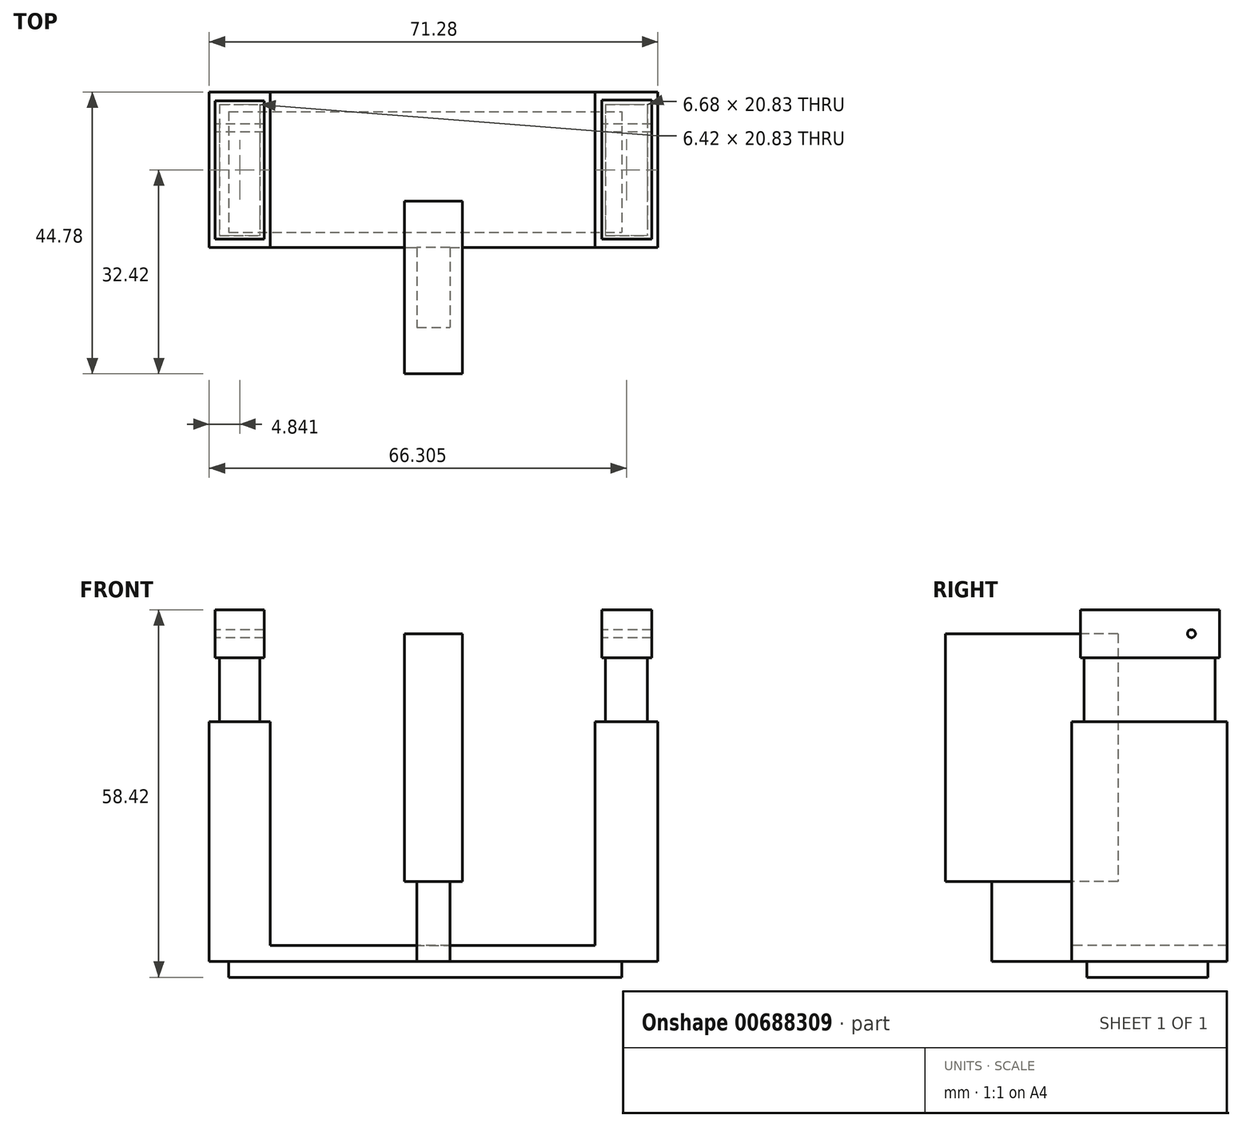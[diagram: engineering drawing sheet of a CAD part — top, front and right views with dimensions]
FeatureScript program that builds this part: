
annotation { "Feature Type Name" : "Feature", "Feature Type Description" : "" }
export const myFeature = defineFeature(function(context is Context, id is Id, definition is map)
    precondition{}
    {
        {
            var Q0;
            Q0=qCreatedBy(makeId("Top.planeOp"),FACE);
            var sketch = newSketch(context, id + "F0", { "sketchPlane" : qUnion([Q0])});
            skLineSegment(sketch, "E0.bottom", {"start": v(0, 0) * mm, "end": v(71.28, 0) * mm});
            skLineSegment(sketch, "E0.top", {"start": v(0, -24.72) * mm, "end": v(33.02, -24.72) * mm});
            skLineSegment(sketch, "E0.left", {"start": v(0, 0) * mm, "end": v(0, -24.72) * mm});
            skLineSegment(sketch, "E0.right", {"start": v(71.28, 0) * mm, "end": v(71.28, -24.72) * mm});
            skLineSegment(sketch, "E1.bottom", {"start": v(3.1, -3.1) * mm, "end": v(65.55, -3.1) * mm});
            skLineSegment(sketch, "E1.top", {"start": v(3.1, -22.32) * mm, "end": v(65.55, -22.32) * mm});
            skLineSegment(sketch, "E1.left", {"start": v(3.1, -3.1) * mm, "end": v(3.1, -22.32) * mm});
            skLineSegment(sketch, "E1.right", {"start": v(65.55, -3.1) * mm, "end": v(65.55, -22.32) * mm});
            skLineSegment(sketch, "E2.bottom", {"start": v(33.02, -24.72) * mm, "end": v(33.02, -24.72) * mm});
            skLineSegment(sketch, "E2.top", {"start": v(33.02, -37.42) * mm, "end": v(38.26, -37.42) * mm});
            skLineSegment(sketch, "E2.left", {"start": v(33.02, -24.72) * mm, "end": v(33.02, -37.42) * mm});
            skLineSegment(sketch, "E2.right", {"start": v(38.26, -24.72) * mm, "end": v(38.26, -37.42) * mm});
            skLineSegment(sketch, "E3", {"start": v(38.26, -24.72) * mm, "end": v(71.28, -24.72) * mm});
            skLineSegment(sketch, "E4", {"start": v(33.02, -24.72) * mm, "end": v(38.26, -24.72) * mm});
            skSolve(sketch);
        }
        {
            var Q0;
            Q0=makeQuery(id+"F0.imprint","IMPRINT",FACE,{"disambiguationData":[TD([[makeQuery(id+"F0.imprint","IMPRINT",EDGE,{"derivedFrom":sQuery(id+"F0.wireOp",EDGE,"E1.bottom")}),-1.0]])]});
            extrude(context, id + "F1", {"entities" : qUnion([Q0]), "depth" : 2.54 * mm, "offsetDistance" : 25.4 * mm});
        }
        {
            var Q0;
            Q0 = qSketchRegion(id + "F0", true);
            var Q1;
            Q1=makeQuery(id+"F1.opExtrude","CAP_FACE",FACE,{"disambiguationData":[OSD([sQuery(id+"F0.wireOp",EDGE,"E1.bottom"),sQuery(id+"F0.wireOp",EDGE,"E1.top"),sQuery(id+"F0.wireOp",EDGE,"E1.left"),sQuery(id+"F0.wireOp",EDGE,"E1.right")])],"isStart":true});
            extrude(context, id + "F2", {"entities" : qUnion([Q0, Q1]), "operationType" : NewBodyOperationType.ADD, "depth" : 2.54 * mm, "offsetDistance" : 25.4 * mm});
        }
        {
            var Q0;
            Q0=makeQuery(id+"F0.imprint","IMPRINT",FACE,{"disambiguationData":[TD([[makeQuery(id+"F0.imprint","IMPRINT",EDGE,{"derivedFrom":sQuery(id+"F0.wireOp",EDGE,"E1.bottom")}),-1.0]])]});
            extrude(context, id + "F3", {"entities" : qUnion([Q0]), "operationType" : NewBodyOperationType.ADD, "oppositeDirection" : true, "depth" : 2.54 * mm, "offsetDistance" : 25.4 * mm});
        }
        {
            var Q0;
            Q0=makeQuery(id+"F0.imprint","IMPRINT",FACE,{"disambiguationData":[TD([[makeQuery(id+"F0.imprint","IMPRINT",EDGE,{"derivedFrom":sQuery(id+"F0.wireOp",EDGE,"E2.top")}),1.0]])]});
            extrude(context, id + "F4", {"entities" : qUnion([Q0]), "operationType" : NewBodyOperationType.ADD, "depth" : 12.7 * mm, "offsetDistance" : 25.4 * mm});
        }
        {
            var Q0;
            {var subQ0=sQuery(id+"F0.wireOp",EDGE,"E1.right");var subQ1=sQuery(id+"F0.wireOp",EDGE,"E1.left");var subQ2=sQuery(id+"F0.wireOp",EDGE,"E1.top");var subQ3=sQuery(id+"F0.wireOp",EDGE,"E1.bottom");Q0=makeQuery(id+"F2.boolean.opBoolean","MERGE",FACE,{"derivedFrom":[makeQuery(id+"F1.opExtrude","CAP_FACE",FACE,{"disambiguationData":[OSD([subQ3,subQ2,subQ1,subQ0])],"isStart":false}),makeQuery(id+"F2.opExtrude","CAP_FACE",FACE,{"disambiguationData":[OSD([sQuery(id+"F0.wireOp",EDGE,"E0.bottom"),sQuery(id+"F0.wireOp",EDGE,"E0.top"),sQuery(id+"F0.wireOp",EDGE,"E0.left"),sQuery(id+"F0.wireOp",EDGE,"E0.right"),subQ3,subQ2,subQ1,subQ0,sQuery(id+"F0.wireOp",EDGE,"E2.top"),sQuery(id+"F0.wireOp",EDGE,"E2.left"),sQuery(id+"F0.wireOp",EDGE,"E2.right"),sQuery(id+"F0.wireOp",EDGE,"E3")])],"isStart":false}),makeQuery(id+"F2.opExtrude","CAP_FACE",FACE,{"disambiguationData":[OSD([subQ3,subQ2,subQ1,subQ0])],"isStart":false})]});}
            var sketch = newSketch(context, id + "F5", { "sketchPlane" : qUnion([Q0])});
            skLineSegment(sketch, "E5", {"start": v(9.68, 0) * mm, "end": v(9.68, -24.72) * mm});
            skLineSegment(sketch, "E6", {"start": v(61.33, 0) * mm, "end": v(61.33, -24.72) * mm});
            skLineSegment(sketch, "E7.bottom", {"start": v(9.68, 0) * mm, "end": v(0, 0) * mm});
            skLineSegment(sketch, "E7.top", {"start": v(9.68, -24.72) * mm, "end": v(0, -24.72) * mm});
            skLineSegment(sketch, "E7.right", {"start": v(0, 0) * mm, "end": v(0, -24.72) * mm});
            skLineSegment(sketch, "E8.bottom", {"start": v(61.33, 0) * mm, "end": v(71.28, 0) * mm});
            skLineSegment(sketch, "E8.top", {"start": v(61.33, -24.72) * mm, "end": v(71.28, -24.72) * mm});
            skLineSegment(sketch, "E8.right", {"start": v(71.28, 0) * mm, "end": v(71.28, -24.72) * mm});
            skSolve(sketch);
        }
        {
            var Q0;
            Q0 = qSketchRegion(id + "F5", true);
            extrude(context, id + "F6", {"entities" : qUnion([Q0]), "operationType" : NewBodyOperationType.ADD, "depth" : 35.56 * mm, "offsetDistance" : 25.4 * mm});
        }
        {
            var Q0;
            Q0=makeQuery(id+"F6.opExtrude","CAP_FACE",FACE,{"disambiguationData":[OSD([sQuery(id+"F5.wireOp",EDGE,"E7.bottom"),sQuery(id+"F5.wireOp",EDGE,"E7.top"),sQuery(id+"F5.wireOp",EDGE,"E5"),sQuery(id+"F5.wireOp",EDGE,"E7.right")])],"isStart":false});
            var sketch = newSketch(context, id + "F7", { "sketchPlane" : qUnion([Q0])});
            skLineSegment(sketch, "E9.bottom", {"start": v(1.63, -1.95) * mm, "end": v(8.05, -1.95) * mm});
            skLineSegment(sketch, "E9.top", {"start": v(1.63, -22.77) * mm, "end": v(8.05, -22.77) * mm});
            skLineSegment(sketch, "E9.left", {"start": v(1.63, -1.95) * mm, "end": v(1.63, -22.77) * mm});
            skLineSegment(sketch, "E9.right", {"start": v(8.05, -1.95) * mm, "end": v(8.05, -22.77) * mm});
            skLineSegment(sketch, "E10", {"start": v(0, 0) * mm, "end": v(1.63, -1.95) * mm});
            skLineSegment(sketch, "E11", {"start": v(8.05, -22.77) * mm, "end": v(9.68, -24.72) * mm});
            skSolve(sketch);
        }
        {
            var Q0;
            Q0=makeQuery(id+"F7.imprint","IMPRINT",FACE,{"disambiguationData":[TD([[makeQuery(id+"F7.imprint","IMPRINT",EDGE,{"derivedFrom":sQuery(id+"F7.wireOp",EDGE,"E9.bottom")}),-1.0]])]});
            extrude(context, id + "F8", {"entities" : qUnion([Q0]), "operationType" : NewBodyOperationType.ADD, "depth" : 10.16 * mm, "offsetDistance" : 25.4 * mm});
        }
        {
            var Q0;
            Q0=makeQuery(id+"F6.opExtrude","CAP_FACE",FACE,{"disambiguationData":[OSD([sQuery(id+"F5.wireOp",EDGE,"E8.bottom"),sQuery(id+"F5.wireOp",EDGE,"E8.top"),sQuery(id+"F5.wireOp",EDGE,"E6"),sQuery(id+"F5.wireOp",EDGE,"E8.right")])],"isStart":false});
            var sketch = newSketch(context, id + "F9", { "sketchPlane" : qUnion([Q0])});
            skLineSegment(sketch, "E12.bottom", {"start": v(62.96, -1.95) * mm, "end": v(69.65, -1.95) * mm});
            skLineSegment(sketch, "E12.top", {"start": v(62.96, -22.77) * mm, "end": v(69.65, -22.77) * mm});
            skLineSegment(sketch, "E12.left", {"start": v(62.96, -1.95) * mm, "end": v(62.96, -22.77) * mm});
            skLineSegment(sketch, "E12.right", {"start": v(69.65, -1.95) * mm, "end": v(69.65, -22.77) * mm});
            skLineSegment(sketch, "E13", {"start": v(61.33, 0) * mm, "end": v(62.96, -1.95) * mm});
            skLineSegment(sketch, "E14", {"start": v(69.65, -22.77) * mm, "end": v(71.28, -24.72) * mm});
            skSolve(sketch);
        }
        {
            var Q0;
            Q0=makeQuery(id+"F9.imprint","IMPRINT",FACE,{"disambiguationData":[TD([[makeQuery(id+"F9.imprint","IMPRINT",EDGE,{"derivedFrom":sQuery(id+"F9.wireOp",EDGE,"E12.bottom")}),-1.0]])]});
            extrude(context, id + "F10", {"entities" : qUnion([Q0]), "operationType" : NewBodyOperationType.ADD, "depth" : 10.16 * mm, "offsetDistance" : 25.4 * mm});
        }
        {
            var Q0;
            Q0=makeQuery(id+"F8.opExtrude","CAP_FACE",FACE,{"disambiguationData":[OSD([sQuery(id+"F7.wireOp",EDGE,"E9.bottom"),sQuery(id+"F7.wireOp",EDGE,"E9.top"),sQuery(id+"F7.wireOp",EDGE,"E9.left"),sQuery(id+"F7.wireOp",EDGE,"E9.right")])],"isStart":false});
            var sketch = newSketch(context, id + "F11", { "sketchPlane" : qUnion([Q0])});
            skLineSegment(sketch, "E15.bottom", {"start": v(0.95, -1.37) * mm, "end": v(8.73, -1.37) * mm});
            skLineSegment(sketch, "E15.top", {"start": v(0.95, -23.35) * mm, "end": v(8.73, -23.35) * mm});
            skLineSegment(sketch, "E15.left", {"start": v(0.95, -1.37) * mm, "end": v(0.95, -23.35) * mm});
            skLineSegment(sketch, "E15.right", {"start": v(8.73, -1.37) * mm, "end": v(8.73, -23.35) * mm});
            skLineSegment(sketch, "E16", {"start": v(0.95, -1.37) * mm, "end": v(1.63, -1.95) * mm});
            skLineSegment(sketch, "E17", {"start": v(8.05, -22.77) * mm, "end": v(8.73, -23.35) * mm});
            skSolve(sketch);
        }
        {
            var Q0;
            Q0=makeQuery(id+"F11.imprint","IMPRINT",FACE,{"disambiguationData":[TD([[makeQuery(id+"F11.imprint","IMPRINT",EDGE,{"derivedFrom":sQuery(id+"F11.wireOp",EDGE,"E15.bottom")}),-1.0]])]});
            var Q1;
            Q1=makeQuery(id+"F11.imprint","IMPRINT",FACE,{"disambiguationData":[TD([[makeQuery(id+"F11.imprint","IMPRINT",EDGE,{"derivedFrom":sQuery(id+"F11.wireOp",EDGE,"E15.top")}),1.0]])]});
            var Q2;
            Q2=makeQuery(id+"F11.imprint","IMPRINT",FACE,{"disambiguationData":[TD([[makeQuery(id+"F11.imprint","IMPRINT",EDGE,{"derivedFrom":makeQuery(id+"F8.opExtrude","CAP_EDGE",EDGE,{"disambiguationData":[OSD([sQuery(id+"F7.wireOp",EDGE,"E9.bottom")])],"isStart":false})}),-1.0]])]});
            extrude(context, id + "F12", {"entities" : qUnion([Q0, Q1, Q2]), "operationType" : NewBodyOperationType.ADD, "depth" : 7.62 * mm, "offsetDistance" : 25.4 * mm});
        }
        {
            var Q0;
            Q0=makeQuery(id+"F10.opExtrude","CAP_FACE",FACE,{"disambiguationData":[OSD([sQuery(id+"F9.wireOp",EDGE,"E12.bottom"),sQuery(id+"F9.wireOp",EDGE,"E12.top"),sQuery(id+"F9.wireOp",EDGE,"E12.left"),sQuery(id+"F9.wireOp",EDGE,"E12.right")])],"isStart":false});
            var sketch = newSketch(context, id + "F13", { "sketchPlane" : qUnion([Q0])});
            skLineSegment(sketch, "E18.bottom", {"start": v(62.4, -1.26) * mm, "end": v(70.33, -1.26) * mm});
            skLineSegment(sketch, "E18.top", {"start": v(62.4, -23.35) * mm, "end": v(70.33, -23.35) * mm});
            skLineSegment(sketch, "E18.left", {"start": v(62.4, -1.26) * mm, "end": v(62.4, -23.35) * mm});
            skLineSegment(sketch, "E18.right", {"start": v(70.33, -1.26) * mm, "end": v(70.33, -23.35) * mm});
            skLineSegment(sketch, "E19", {"start": v(62.4, -1.26) * mm, "end": v(62.96, -1.95) * mm});
            skLineSegment(sketch, "E20", {"start": v(69.65, -22.77) * mm, "end": v(70.33, -23.35) * mm});
            skSolve(sketch);
        }
        {
            var Q0;
            Q0=makeQuery(id+"F13.imprint","IMPRINT",FACE,{"disambiguationData":[TD([[makeQuery(id+"F13.imprint","IMPRINT",EDGE,{"derivedFrom":sQuery(id+"F13.wireOp",EDGE,"E18.bottom")}),-1.0]])]});
            var Q1;
            Q1=makeQuery(id+"F13.imprint","IMPRINT",FACE,{"disambiguationData":[TD([[makeQuery(id+"F13.imprint","IMPRINT",EDGE,{"derivedFrom":sQuery(id+"F13.wireOp",EDGE,"E18.top")}),1.0]])]});
            var Q2;
            Q2=makeQuery(id+"F13.imprint","IMPRINT",FACE,{"disambiguationData":[TD([[makeQuery(id+"F13.imprint","IMPRINT",EDGE,{"derivedFrom":makeQuery(id+"F10.opExtrude","CAP_EDGE",EDGE,{"disambiguationData":[OSD([sQuery(id+"F9.wireOp",EDGE,"E12.bottom")])],"isStart":false})}),-1.0]])]});
            extrude(context, id + "F14", {"entities" : qUnion([Q0, Q1, Q2]), "operationType" : NewBodyOperationType.ADD, "depth" : 7.62 * mm, "offsetDistance" : 25.4 * mm});
        }
        {
            var Q0;
            Q0=makeQuery(id+"F12.opExtrude","SWEPT_FACE",FACE,{"disambiguationData":[OSD([sQuery(id+"F11.wireOp",EDGE,"E15.left")])]});
            var sketch = newSketch(context, id + "F15", { "sketchPlane" : qUnion([Q0])});
            skLineSegment(sketch, "E21", {"start": v(5.7, 55.88) * mm, "end": v(5.7, 48.26) * mm});
            skLineSegment(sketch, "E22", {"start": v(1.37, 52.07) * mm, "end": v(5.7, 52.07) * mm});
            skSolve(sketch);
        }
        {
            var Q0;
            Q0=sQuery(id+"F15.wireOp",VERTEX,"E22.end");
            var Q1;
            Q1=makeQuery(id+"F1.opExtrude","SWEPT_BODY",BODY,{"disambiguationData":[OSD([sQuery(id+"F0.wireOp",EDGE,"E1.bottom"),sQuery(id+"F0.wireOp",EDGE,"E1.top"),sQuery(id+"F0.wireOp",EDGE,"E1.left"),sQuery(id+"F0.wireOp",EDGE,"E1.right")])]});
            hole(context, id + "F16", {"style" : HoleStyle.SIMPLE, "endStyle" : HoleEndStyle.BLIND, "holeDiameter" : 1.27 * mm, "majorDiameter" : 6.35 * mm, "holeDepth" : 127 * mm, "isTappedThrough" : true, "tappedDepth" : 12.7 * mm, "tapClearance" : 3, "locations" : qUnion([Q0]), "scope" : qUnion([Q1])});
        }
        {
            var Q0;
            Q0=makeQuery(id+"F4.opExtrude","CAP_FACE",FACE,{"disambiguationData":[OSD([sQuery(id+"F0.wireOp",EDGE,"E2.top"),sQuery(id+"F0.wireOp",EDGE,"E2.left"),sQuery(id+"F0.wireOp",EDGE,"E2.right"),sQuery(id+"F0.wireOp",EDGE,"E4")])],"isStart":false});
            var sketch = newSketch(context, id + "F17", { "sketchPlane" : qUnion([Q0])});
            skLineSegment(sketch, "E23.bottom", {"start": v(31.05, -17.36) * mm, "end": v(40.23, -17.36) * mm});
            skLineSegment(sketch, "E23.top", {"start": v(31.05, -44.78) * mm, "end": v(40.23, -44.78) * mm});
            skLineSegment(sketch, "E23.left", {"start": v(31.05, -17.36) * mm, "end": v(31.05, -44.78) * mm});
            skLineSegment(sketch, "E23.right", {"start": v(40.23, -17.36) * mm, "end": v(40.23, -44.78) * mm});
            skLineSegment(sketch, "E24", {"start": v(31.05, -17.36) * mm, "end": v(33.02, -24.72) * mm});
            skLineSegment(sketch, "E25", {"start": v(38.26, -37.42) * mm, "end": v(40.23, -44.78) * mm});
            skSolve(sketch);
        }
        {
            var Q0;
            Q0=makeQuery(id+"F17.imprint","IMPRINT",FACE,{"disambiguationData":[TD([[makeQuery(id+"F17.imprint","IMPRINT",EDGE,{"derivedFrom":sQuery(id+"F17.wireOp",EDGE,"E23.bottom")}),-1.0]])]});
            var Q1;
            Q1=makeQuery(id+"F17.imprint","IMPRINT",FACE,{"disambiguationData":[TD([[makeQuery(id+"F17.imprint","IMPRINT",EDGE,{"derivedFrom":sQuery(id+"F17.wireOp",EDGE,"E23.top")}),1.0]])]});
            var Q2;
            Q2=makeQuery(id+"F17.imprint","IMPRINT",FACE,{"disambiguationData":[TD([[makeQuery(id+"F17.imprint","IMPRINT",EDGE,{"derivedFrom":makeQuery(id+"F4.opExtrude","CAP_EDGE",EDGE,{"disambiguationData":[OSD([sQuery(id+"F0.wireOp",EDGE,"E2.top")])],"isStart":false})}),1.0]])]});
            extrude(context, id + "F18", {"entities" : qUnion([Q0, Q1, Q2]), "operationType" : NewBodyOperationType.ADD, "depth" : 39.37 * mm, "offsetDistance" : 25.4 * mm});
        }
    });
